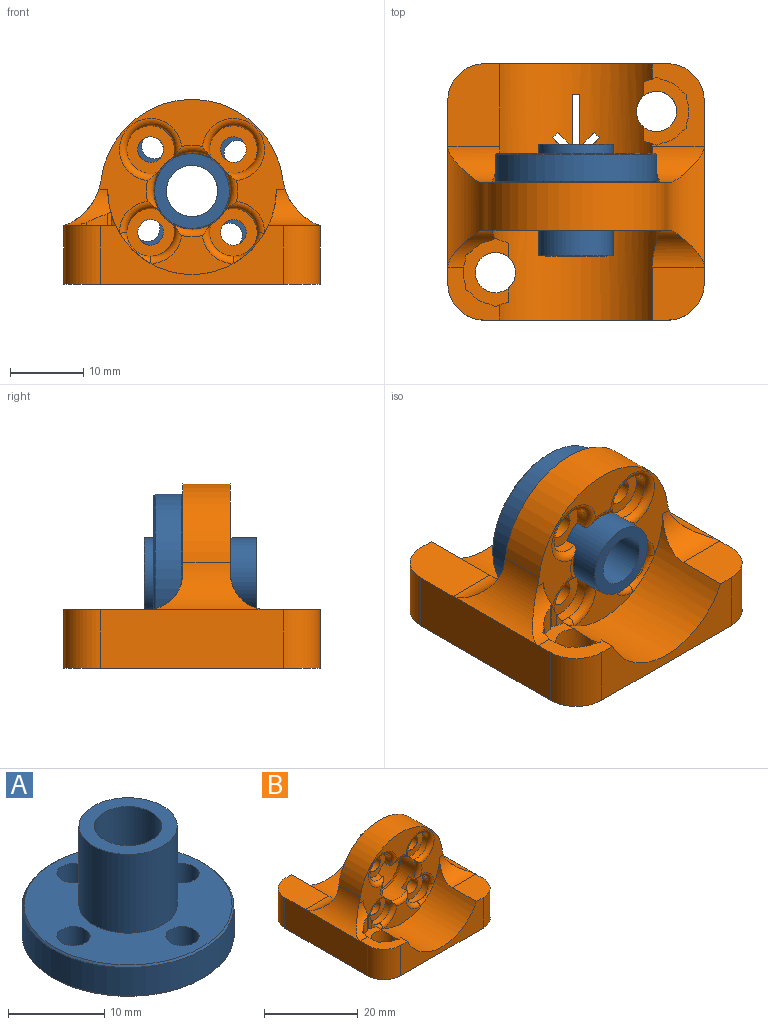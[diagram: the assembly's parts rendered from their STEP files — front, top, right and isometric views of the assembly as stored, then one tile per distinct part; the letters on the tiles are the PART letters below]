
ASSEMBLY  parts=2 mates=1
PART A: 14 faces, bbox 22x22x15.3 mm
  f0: plane 21.63x21.63mm, normal (0,0,-1), area 247.4mm2, adj f7,f8,f10,f11,f12,f13
  f1: plane 21.63x21.63mm, normal (0,0,1), area 248.2mm2, adj f5,f9,f10,f11,f12,f13
  f2: cylinder r=11.01mm len=22.03mm, axis (0,0,-1), area 249.1mm2, adj f8,f9
  f3: cylinder r=3.5mm len=15.25mm, axis (0,0,-1), area 335.4mm2, adj f4,f6
  f4: plane 10.2x10.2mm, normal (0,0,1), area 43.2mm2, adj f3,f5
  f5: cylinder r=5.1mm len=10.2mm, axis (0,0,-1), area 320.4mm2, adj f1,f4
  f6: plane 10.25x10.25mm, normal (0,0,-1), area 44mm2, adj f3,f7
  f7: cylinder r=5.12mm len=10.25mm, axis (0,0,1), area 40.3mm2, adj f0,f6
  f8: cone r=11.01mm half-angle=45deg, axis (0,0,1), area 19.4mm2, adj f0,f2
  f9: cone r=10.81mm half-angle=45deg, axis (0,0,-1), area 19.4mm2, adj f1,f2
  f10: cylinder r=1.72mm len=4mm, axis (0,0,1), area 43.4mm2, adj f0,f1
  f11: cylinder r=1.72mm len=4mm, axis (0,0,1), area 43.4mm2, adj f0,f1
  f12: cylinder r=1.72mm len=4mm, axis (0,0,1), area 43.4mm2, adj f0,f1
  f13: cylinder r=1.72mm len=4mm, axis (0,0,1), area 43.4mm2, adj f0,f1
PART B: 90 faces, bbox 35x35x25.3 mm
  f0: plane 11.33x5.32mm, normal (0,-1,0), area 29.6mm2, adj f19,f78,f80,f82
  f1: cylinder r=11.5mm len=23mm, axis (0,-1,0), area 396.1mm2, adj f15,f17,f20,f24,f27,f38,f45,f46
  f2: plane 35x35mm, normal (0,0,-1), area 1140.6mm2, adj f17,f18,f21,f22,f23,f24,f56,f57
  f3: cylinder r=5.25mm len=10.5mm, axis (0,1,0), area 131.6mm2, adj f60,f61,f62,f63,f64,f65,f66,f67
  f4: cylinder r=1.75mm len=4mm, axis (0,1,0), area 44mm2, adj f27,f61
  f5: cylinder r=1.75mm len=4mm, axis (0,1,0), area 44mm2, adj f27,f67
  f6: cylinder r=1.75mm len=4mm, axis (0,1,0), area 44mm2, adj f27,f63
  f7: cylinder r=1.75mm len=4mm, axis (0,1,0), area 44mm2, adj f27,f65
  f8: plane 25.43x18.24mm, normal (0,-1,0), area 123.4mm2, adj f19,f26,f28,f29,f52,f53,f79,f81
  f9: plane 3.88x0.61mm, normal (0.5,-0.87,0), area 2.6mm2, adj f19,f31,f32,f49,f52
  f10: plane 2.26x0.69mm, normal (1,0,0), area 1.5mm2, adj f32,f33,f48,f52
  f11: plane 2x0.6mm, normal (0.5,0.87,0), area 1.4mm2, adj f16,f32,f34,f47
  f12: plane 2x0.54mm, normal (-0.5,-0.87,0), area 1.2mm2, adj f15,f38,f41,f44
  f13: plane 2x0.54mm, normal (-0.5,0.87,0), area 1.2mm2, adj f15,f37,f38,f43
  f14: plane 2x0.62mm, normal (-1,0,0), area 1.2mm2, adj f15,f38,f40,f42
  f15: plane 11.25x7.07mm, normal (0,0,1), area 38.2mm2, adj f1,f12,f13,f14,f23,f24,f36,f37
  f16: plane 7.25x7.07mm, normal (0,0,1), area 24.1mm2, adj f11,f19,f21,f22,f30,f34,f35,f47
  f17: cylinder r=2.75mm len=6mm, axis (0,0,-1), area 99.9mm2, adj f1,f2,f38
  f18: cylinder r=2.75mm len=6mm, axis (0,0,-1), area 99.9mm2, adj f2,f19,f32
  f19: cylinder r=11.5mm len=23mm, axis (0,-1,0), area 304.8mm2, adj f0,f8,f9,f16,f18,f22,f25,f30
  f20: plane 11.25x7.07mm, normal (0,0,1), area 74.2mm2, adj f1,f21,f24,f54,f59
  f21: plane 25x8mm, normal (-1,0,0), area 200mm2, adj f2,f16,f20,f28,f56,f59
  f22: plane 25x8mm, normal (0,-1,0), area 100.4mm2, adj f2,f16,f19,f25,f56,f57
  f23: plane 25x8mm, normal (1,0,0), area 200mm2, adj f2,f15,f25,f29,f57,f58
  f24: plane 25x8mm, normal (0,1,0), area 100.4mm2, adj f1,f2,f15,f20,f58,f59
  f25: plane 7.25x7.07mm, normal (0,0,1), area 45.9mm2, adj f19,f22,f23,f53,f57
  f26: cylinder r=12.5mm len=24.78mm, axis (0,1,0), area 233.5mm2, adj f8,f27,f28,f29
  f27: plane 25.43x23.9mm, normal (0,1,0), area 289.4mm2, adj f1,f4,f5,f6,f7,f26,f28,f29
  f28: cylinder r=8mm len=16.5mm, axis (0,-1,0), area 75.9mm2, adj f8,f21,f26,f27,f52,f54
  f29: cylinder r=8mm len=16.5mm, axis (0,-1,0), area 75.9mm2, adj f8,f23,f26,f27,f53,f55
  f30: plane 2x0.6mm, normal (-0.5,0.87,0), area 1.4mm2, adj f16,f19,f32,f35,f51
  f31: plane 3.53x0.63mm, normal (-0.5,-0.87,0), area 1.8mm2, adj f9,f19,f32,f50
  f32: plane 9.41x6.16mm, normal (0,0,1), area 25.3mm2, adj f9,f10,f11,f18,f19,f30,f31,f33
  f33: plane 2.4x0.6mm, normal (0.5,-0.87,0), area 1.6mm2, adj f10,f32,f49,f52
  f34: plane 2x0.69mm, normal (1,0,0), area 1.4mm2, adj f11,f16,f32,f48
  f35: plane 2x0.6mm, normal (0.5,0.87,0), area 1.4mm2, adj f16,f30,f32,f47
  f36: plane 2x0.54mm, normal (0.5,-0.87,0), area 1.2mm2, adj f15,f38,f39,f46
  f37: plane 2x0.54mm, normal (0.5,0.87,0), area 1.2mm2, adj f13,f15,f38,f45
  f38: plane 9.35x6.16mm, normal (0,0,1), area 25.2mm2, adj f1,f12,f13,f14,f17,f36,f37,f39
  f39: plane 2x0.54mm, normal (-0.5,-0.87,0), area 1.2mm2, adj f15,f36,f38,f44
  f40: plane 2x0.54mm, normal (-0.5,0.87,0), area 1.2mm2, adj f14,f15,f38,f43
  f41: plane 2x0.62mm, normal (-1,0,0), area 1.2mm2, adj f12,f15,f38,f42
  f42: cylinder r=4.4mm len=3.44mm, axis (0,0,1), area 7.1mm2, adj f14,f15,f38,f41
  f43: cylinder r=4.4mm len=2.98mm, axis (0,0,1), area 7.1mm2, adj f13,f15,f38,f40
  f44: cylinder r=4.4mm len=2.98mm, axis (0,0,1), area 7.1mm2, adj f12,f15,f38,f39
  f45: cylinder r=4.4mm len=2mm, axis (0,0,1), area 1.2mm2, adj f1,f15,f37,f38
  f46: cylinder r=4.4mm len=2mm, axis (0,0,1), area 1.2mm2, adj f1,f15,f36,f38
  f47: cylinder r=4.4mm len=2.87mm, axis (0,0,1), area 6.8mm2, adj f11,f16,f32,f35
  f48: cylinder r=4.4mm len=3.32mm, axis (0,0,1), area 6.8mm2, adj f10,f16,f32,f34,f52
  f49: cylinder r=4.4mm len=3.54mm, axis (0,0,1), area 10.1mm2, adj f9,f32,f33,f52
  f50: cylinder r=4.4mm len=1.94mm, axis (0,0,1), area 1.2mm2, adj f19,f31,f32
  f51: cylinder r=4.4mm len=1.94mm, axis (0,0,1), area 1.2mm2, adj f19,f30,f32
  f52: cylinder r=5mm len=6.39mm, axis (-1,0,0), area 18.1mm2, adj f8,f9,f10,f16,f19,f28,f33,f48
  f53: cylinder r=5mm len=7.07mm, axis (-1,0,0), area 32.7mm2, adj f8,f19,f25,f29
  f54: cylinder r=5mm len=7.07mm, axis (1,0,0), area 32.7mm2, adj f1,f20,f27,f28
  f55: cylinder r=5mm len=7.07mm, axis (1,0,0), area 32.7mm2, adj f1,f15,f27,f29
  f56: cylinder r=5mm len=8mm, axis (0,0,-1), area 62.8mm2, adj f2,f16,f21,f22
  f57: cylinder r=5mm len=8mm, axis (0,0,1), area 62.8mm2, adj f2,f22,f23,f25
  f58: cylinder r=5mm len=8mm, axis (0,0,-1), area 62.8mm2, adj f2,f15,f23,f24
  f59: cylinder r=5mm len=8mm, axis (0,0,1), area 62.8mm2, adj f2,f20,f21,f24
  f60: cylinder r=3.25mm len=6.5mm, axis (0,-1,0), area 26.3mm2, adj f3,f61,f83
  f61: plane 6.5x6.5mm, normal (0,-1,0), area 22.6mm2, adj f3,f4,f60
  f62: cylinder r=3.25mm len=6.5mm, axis (0,-1,0), area 27.4mm2, adj f3,f63,f82,f84,f86
  f63: plane 6.5x6.5mm, normal (0,-1,0), area 22.6mm2, adj f3,f6,f62
  f64: cylinder r=3.25mm len=6.5mm, axis (0,-1,0), area 26.3mm2, adj f3,f65,f87
  f65: plane 6.5x6.5mm, normal (0,-1,0), area 22.6mm2, adj f3,f7,f64
  f66: cylinder r=3.25mm len=6.5mm, axis (0,-1,0), area 27.4mm2, adj f3,f67,f77,f78,f79
  f67: plane 6.5x6.5mm, normal (0,-1,0), area 22.6mm2, adj f3,f5,f66
  f68: plane 1.8x0.71mm, normal (-0.71,-0.71,0), area 1.7mm2, adj f1,f2,f69,f76
  f69: plane 3.21x3.21mm, normal (-0.71,0.71,0), area 6.7mm2, adj f1,f2,f68,f70
  f70: plane 3.21x3.21mm, normal (0.71,0.71,0), area 6.7mm2, adj f1,f2,f69,f71
  f71: plane 1.8x0.71mm, normal (0.71,-0.71,0), area 1.7mm2, adj f1,f2,f70,f72
  f72: plane 1.99x1.99mm, normal (-0.71,-0.71,0), area 4.1mm2, adj f1,f2,f71,f73
  f73: plane 7.19x1.36mm, normal (1,0,0), area 9.8mm2, adj f1,f2,f72,f74
  f74: plane 1.36x1mm, normal (0,-1,0), area 1.4mm2, adj f1,f2,f73,f75
  f75: plane 7.19x1.36mm, normal (-1,0,0), area 9.8mm2, adj f1,f2,f74,f76
  f76: plane 1.99x1.99mm, normal (0.71,-0.71,0), area 4.1mm2, adj f1,f2,f68,f75
  f77: bspline ~4.68x4.5mm, area 5.1mm2, adj f19,f66,f78,f79
  f78: torus R=4.25mm, axis (0,-1,0), area 9.6mm2, adj f0,f66,f77,f80
  f79: torus R=4.25mm, axis (0,-1,0), area 9.7mm2, adj f8,f66,f77,f81
  f80: torus R=6.25mm, axis (0,-1,0), area 6.5mm2, adj f0,f3,f78,f82
  f81: torus R=6.25mm, axis (0,-1,0), area 6.5mm2, adj f3,f8,f79,f83
  f82: torus R=4.25mm, axis (0,-1,0), area 9.6mm2, adj f0,f62,f80,f84
  f83: torus R=4.25mm, axis (0,-1,0), area 28mm2, adj f8,f60,f81,f85
  f84: bspline ~4.24x4.19mm, area 5.1mm2, adj f19,f62,f82,f86
  f85: torus R=6.25mm, axis (0,-1,0), area 6.5mm2, adj f3,f8,f83,f87
  f86: torus R=4.25mm, axis (0,-1,0), area 9.7mm2, adj f8,f62,f84,f88
  f87: torus R=4.25mm, axis (0,-1,0), area 28mm2, adj f8,f64,f85,f88
  f88: torus R=6.25mm, axis (0,-1,0), area 6.5mm2, adj f3,f8,f86,f87
  f89: torus R=6.25mm, axis (0,-1,0), area 55.4mm2, adj f3,f27
PLACE A rot(axis=(0.89,-0.32,0.32),96.8deg) t=(0,5.25,12.75)mm
PLACE B at identity fixed
MATE planar B.f27 <-> A.f2  axis (0,1,0) through (0,1.25,13.82)mm
